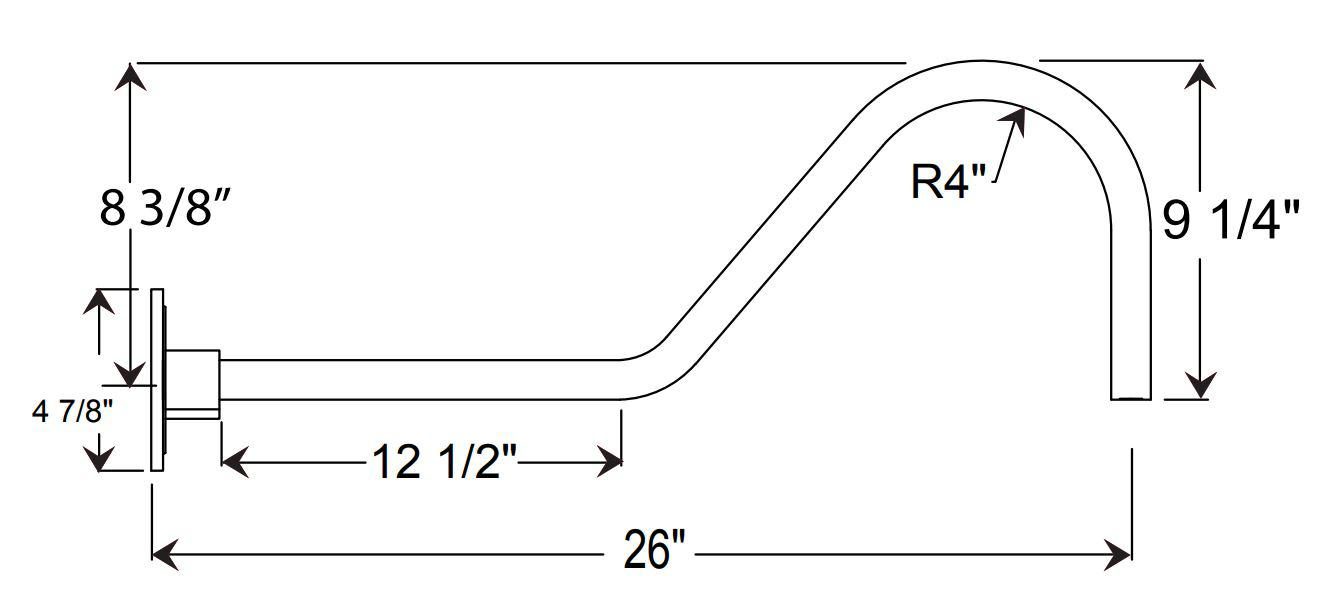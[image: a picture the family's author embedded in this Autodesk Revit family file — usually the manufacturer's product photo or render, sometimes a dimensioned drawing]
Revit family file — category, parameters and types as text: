
# Revit family: Vaportite Pendant (VTP)LED
name_source: partatom
category: Lighting Fixtures
units: mm (PartAtom-declared; Revit-internal decimal feet)

## family parameters
Always vertical = Yes
Cut with Voids When Loaded = No
Light Source = Yes
OmniClass Number = 23.80.70.00
OmniClass Title = Lighting
Part Type = Normal
Room Calculation Point = No
Round Connector Dimension = Use Diameter
Shared = No
Work Plane-Based = No

## types (1)
- VTP200GL
    Apparent Load = 12 VA
    BULB = Yes
    Body Colour = Spun aluminium
    Body Material = body
    Bulb = Bulb
    CRI = >90
    Color Filter = 16777215
    Construction Material = Heavy Duty spun aluminum.
    Default Elevation = 0' - 0"
    Description = 120-277 Voltage
    Dimming = 1%
    Dimming Lamp Color Temperature Shift = <None>
    Efficiency = 65-125 lumens per watt
    Fixture Diameter = 0' - 5 1/4"
    Fixture Height = 1' - 1 1/2"
    HUB = Texture Black
    Lamp = LED
    Life = L70 50,000 hours
    Load Classification = Lighting
    Manufacturer = ANP Lighting
    Model = VTP200GL
    Photometric Web File = VTP200GLCL-M021LDNW40K.IES
    Power Factor = 1
    Tilt Angle = 90.00°
    URL = https://www.anplighting.com
    VTP200GL = Yes
    Voltage = 120 V
    Warranty = 5 year limited warranty
    Wattage Comments = 12 W
    Weight = 5.0 lb
    a = 1' - 0"
    b = 0' - 2"

## geometry (parser evidence)
native form markers: Sweep x22
no freeform markers — native parametric forms only
